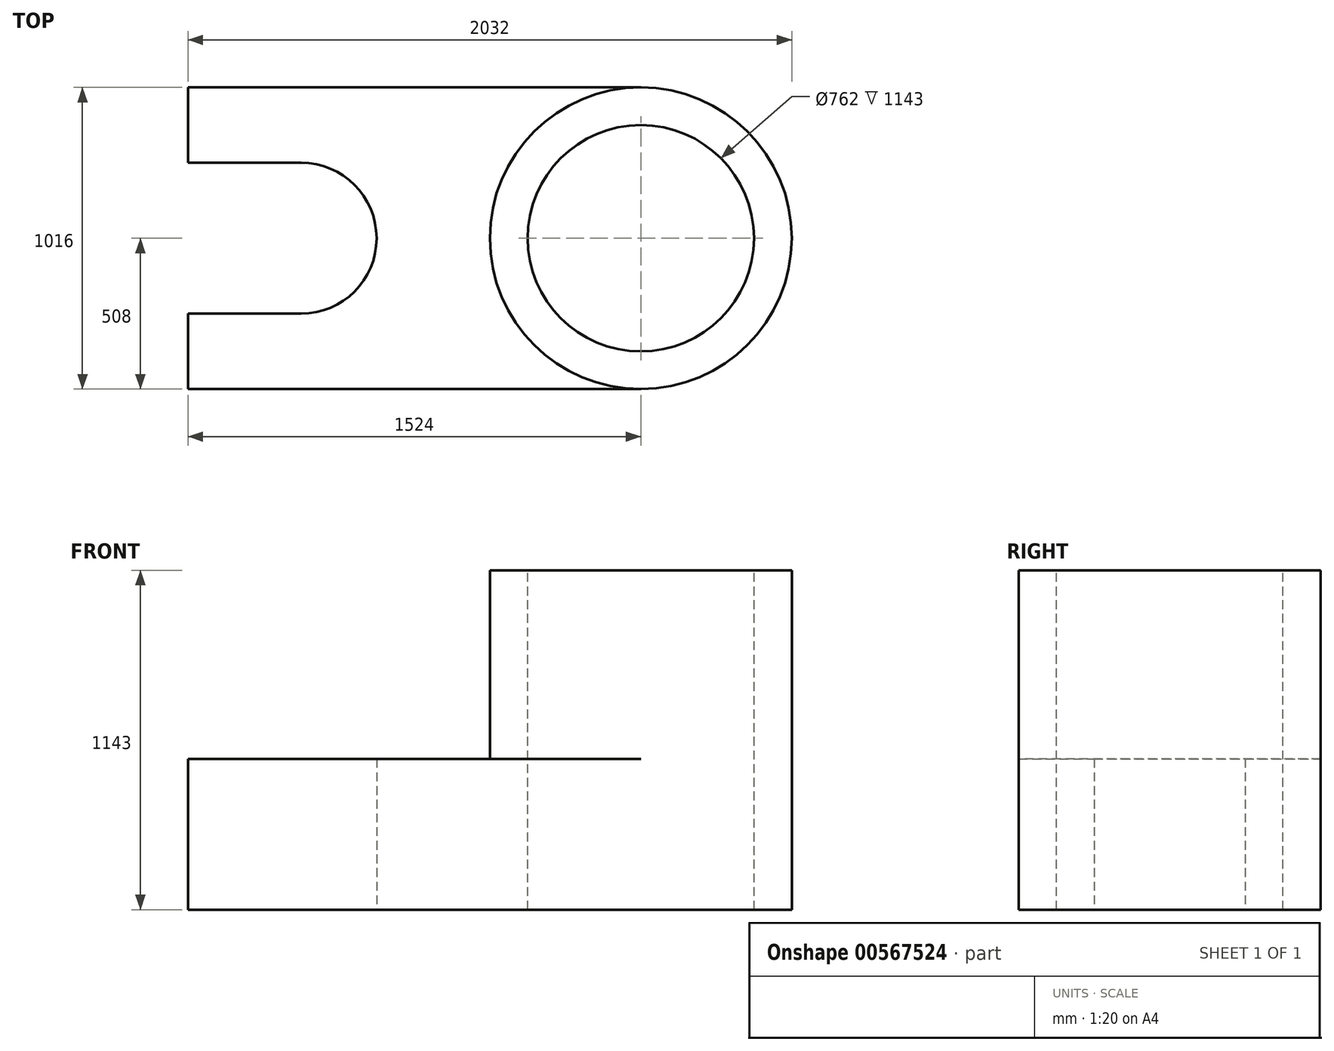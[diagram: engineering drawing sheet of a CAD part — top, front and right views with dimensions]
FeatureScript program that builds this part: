
annotation { "Feature Type Name" : "Feature", "Feature Type Description" : "" }
export const myFeature = defineFeature(function(context is Context, id is Id, definition is map)
    precondition{}
    {
        {
            var Q0;
            Q0=qCreatedBy(makeId("Top.planeOp"),FACE);
            var sketch = newSketch(context, id + "F0", { "sketchPlane" : qUnion([Q0])});
            skLineSegment(sketch, "E0.bottom", {"start": v(762, -508) * mm, "end": v(-762, -508) * mm});
            skLineSegment(sketch, "E0.top", {"start": v(762, 508) * mm, "end": v(-762, 508) * mm});
            skLineSegment(sketch, "E0.right", {"start": v(-762, -508) * mm, "end": v(-762, -254) * mm});
            skPoint(sketch, "E0.middle", {"position": v(0, 0) * mm});
            skArc(sketch, "E1", {"start": v(762, -508) * mm, "mid": v(1270, 0) * mm, "end": v(762, 508) * mm});
            skArc(sketch, "E2", {"start": v(-381, -254) * mm, "mid": v(-127, 0) * mm, "end": v(-381, 254) * mm});
            skLineSegment(sketch, "E3", {"start": v(-381, 254) * mm, "end": v(-762, 254) * mm});
            skLineSegment(sketch, "E4", {"start": v(-381, -254) * mm, "end": v(-762, -254) * mm});
            skLineSegment(sketch, "E5.trimOffspring", {"start": v(-762, 254) * mm, "end": v(-762, 508) * mm});
            skSolve(sketch);
        }
        {
            var Q0;
            Q0=makeQuery(id+"F0.imprint","IMPRINT",FACE,{"disambiguationData":[TD([[makeQuery(id+"F0.imprint","IMPRINT",EDGE,{"derivedFrom":sQuery(id+"F0.wireOp",EDGE,"E0.bottom")}),-1.0]])]});
            extrude(context, id + "F1", {"entities" : qUnion([Q0]), "depth" : 508 * mm, "offsetDistance" : 25.4 * mm});
        }
        {
            var Q0;
            Q0=makeQuery(id+"F1.opExtrude","CAP_FACE",FACE,{"disambiguationData":[OSD([sQuery(id+"F0.wireOp",EDGE,"E0.bottom"),sQuery(id+"F0.wireOp",EDGE,"E0.top"),sQuery(id+"F0.wireOp",EDGE,"E0.right"),sQuery(id+"F0.wireOp",EDGE,"E1"),sQuery(id+"F0.wireOp",EDGE,"E2"),sQuery(id+"F0.wireOp",EDGE,"E3"),sQuery(id+"F0.wireOp",EDGE,"E4"),sQuery(id+"F0.wireOp",EDGE,"E5.trimOffspring")])],"isStart":false});
            var sketch = newSketch(context, id + "F2", { "sketchPlane" : qUnion([Q0])});
            skCircle(sketch, "E6", {"center": v(762, 0) * mm, "radius": 508 * mm});
            skSolve(sketch);
        }
        {
            var Q0;
            {var subQ0=sQuery(id+"F2.wireOp",EDGE,"E6");var subQ1=makeQuery(id+"F2.imprint","INTERSECT",VERTEX,{"derivedFrom":[makeQuery(id+"F1.opExtrude","CAP_EDGE",EDGE,{"disambiguationData":[OSD([sQuery(id+"F0.wireOp",EDGE,"E0.bottom")])],"isStart":false}),subQ0]});Q0=makeQuery(id+"F2.imprint","IMPRINT",FACE,{"disambiguationData":[TD([[makeQuery(id+"F2.imprint","IMPRINT",EDGE,{"disambiguationData":[TD([[subQ1,-1.0]])],"derivedFrom":subQ0}),1.0]])]});}
            extrude(context, id + "F3", {"entities" : qUnion([Q0]), "operationType" : NewBodyOperationType.ADD, "depth" : 635 * mm, "offsetDistance" : 25.4 * mm});
        }
        {
            var Q0;
            Q0=makeQuery(id+"F3.opExtrude","CAP_FACE",FACE,{"disambiguationData":[OSD([sQuery(id+"F2.wireOp",EDGE,"E6")])],"isStart":false});
            var sketch = newSketch(context, id + "F4", { "sketchPlane" : qUnion([Q0])});
            skCircle(sketch, "E7", {"center": v(762, 0) * mm, "radius": 381 * mm});
            skSolve(sketch);
        }
        {
            var Q0;
            Q0=makeQuery(id+"F4.imprint","IMPRINT",FACE,{"disambiguationData":[TD([[makeQuery(id+"F4.imprint","IMPRINT",EDGE,{"derivedFrom":sQuery(id+"F4.wireOp",EDGE,"E7")}),1.0]])]});
            extrude(context, id + "F5", {"entities" : qUnion([Q0]), "operationType" : NewBodyOperationType.REMOVE, "oppositeDirection" : true, "depth" : 1143 * mm, "offsetDistance" : 25.4 * mm});
        }
    });
